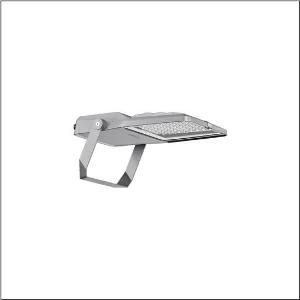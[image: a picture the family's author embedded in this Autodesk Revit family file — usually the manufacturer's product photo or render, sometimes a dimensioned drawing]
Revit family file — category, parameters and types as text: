
# Revit family: floodlight_fl_21_iq_mini___pl43_5xa7771c2a1a_27d2
name_source: partatom
category: Lighting Fixtures
units: mm (PartAtom-declared; Revit-internal decimal feet)

## family parameters
Cut with Voids When Loaded = No
Host = Face
Light Source = No
Part Type = Normal
Room Calculation Point = No
Round Connector Dimension = Use Diameter
Shared = No

## types (1)
- --- (1 x LED, 12520 lm, 87.2 W, 3000K)
    Apparent Load = 87 VA
    CIE Flux Codes = 27 78 99 100 100
    Color Rendering = 70
    Color Temperature = 3000K
    Default Elevation = 1800 mm
    Description = Floodlight FL 21 iQ mini, floodlight, primary light control with lens, of PMMA, primary optical cover: protective disc, of toughened safety glass, transparent, light distribution: PL43, light emission: direct distribution, installation type: surface-mounted, LED, High Power LED, rated luminous flux: 12.520lm, luminous efficacy: 144lm/W, light colour: 730, colour temperature: 3000K, control: Auto-Match, Temp-Guard, Lumen-Switch, Night-Set, Smart-Wire, Light-Fading, Desk-Remote (wireless, voltage-free reading and setting of iQ features in the workshop via application-optimized NFC function/RFID function), optimised constant luminous flux control (CLO 2.0), with terminal, 6-pole, mains connection: 220..240V, AC, 50/60Hz, start of lifetime: 87W, end of service life: 92W, reduction: 40W, luminaire housing, of diecast aluminium, powder-coated, Siteco® metallic grey (DB 702S), corrosivity category C5 mid according to DIN EN ISO 12944, sealing non-destructively replaceable, mounting bracket, of steel, galvanised, powder-coated, Siteco® metallic grey (DB 702S), protection rating (complete): IP66, insulation class (complete): insulation class II (safety insulation), certification: CE, ENEC, VDE, protection symbol: D, impact resistance: IK08, permissible operating ambient temperature: -40..+40°C, permissible operating ambient temperature for outdoor applications: -40..+50°C, standard: DIN EN 12944, LABS conformity tested according to VDMA 24364:2018-05, packaging unit: 1 piece

Light Distribution: PL43
    Height = 70 mm
    Lamp = 1 x LED
    Lamp Light Flux = 12520 lm
    Lamp Power = 87.2 W
    Lamp count = 1
    Length = 485 mm
    Luminous efficacy = 144 lm/W
    Manufacturer = Siteco
    ModVariant = No
    Model = 5XA7771C2A1A
    Number of Poles = 1
    OnlyDefault = Yes
    Power Factor = 1
    Product Name = Floodlight FL 21 iQ mini | PL43
    Product group = floodlight | pylon annexe
    ProductGroupID = 6200
    Protection Class = Protection class II
    Protection Degree = IP 66
    RLX_Detail_Level = 1
    RLX_Emergency_Light_Flux = 0 lm
    RLX_Emergency_Type = 0
    RLX_Emergency_Type_DB = No
    RlxData = <blob elided: 96201 chars, md5=9e0b192e>
    Socket = socket
    Standby Power = 0 W
    System Light Flux = 12520 lm
    System Power = 87 W
    Type Comments = factory setting: luminous flux: 100 % | dim-lin: 254 | 456 mA
    Type Image = l_1006845.jpg
    URL = http://relux.com
    VarID = @adj_112761
    Voltage = 0 V
    Weight = 0.00 kg
    Width = 337 mm

## geometry (parser evidence)
native form markers: Blend x4, Sweep x13
no freeform markers — native parametric forms only
